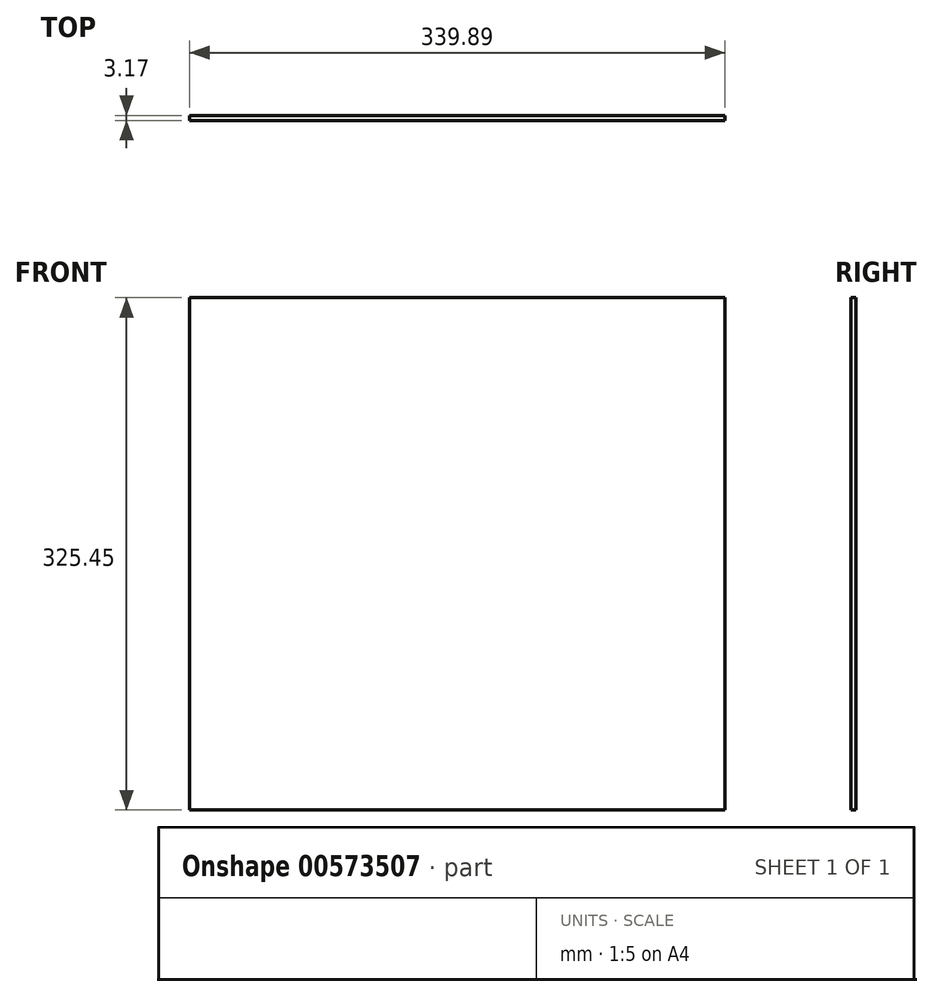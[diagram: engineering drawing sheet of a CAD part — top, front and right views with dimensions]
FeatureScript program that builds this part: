
annotation { "Feature Type Name" : "Feature", "Feature Type Description" : "" }
export const myFeature = defineFeature(function(context is Context, id is Id, definition is map)
    precondition{}
    {
        {
            var Q0;
            Q0=qCreatedBy(makeId("Front.planeOp"),FACE);
            var sketch = newSketch(context, id + "F0", { "sketchPlane" : qUnion([Q0])});
            skLineSegment(sketch, "E0.bottom", {"start": v(660.23, 0) * mm, "end": v(1000.13, 0) * mm});
            skLineSegment(sketch, "E0.top", {"start": v(660.23, 325.45) * mm, "end": v(1000.13, 325.45) * mm});
            skLineSegment(sketch, "E0.left", {"start": v(660.23, 0) * mm, "end": v(660.23, 325.45) * mm});
            skLineSegment(sketch, "E0.right", {"start": v(1000.13, 0) * mm, "end": v(1000.13, 325.45) * mm});
            skSolve(sketch);
        }
        {
            var Q0;
            Q0=makeQuery(id+"F0.imprint","IMPRINT",FACE,{"disambiguationData":[TD([[makeQuery(id+"F0.imprint","IMPRINT",EDGE,{"derivedFrom":sQuery(id+"F0.wireOp",EDGE,"E0.bottom")}),1.0]])]});
            extrude(context, id + "F1", {"entities" : qUnion([Q0]), "depth" : 3.17 * mm, "offsetDistance" : 25.4 * mm});
        }
    });
